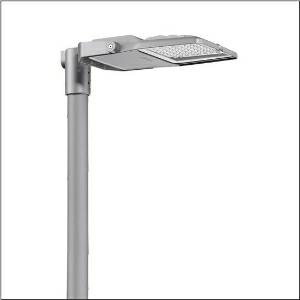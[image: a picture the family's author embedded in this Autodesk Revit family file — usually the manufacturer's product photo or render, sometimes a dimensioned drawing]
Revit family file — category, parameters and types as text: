
# Revit family: floodlight_fl_21_mini___pl61_5xa7776c2c3a_9e20
name_source: partatom
category: Lighting Fixtures
units: mm (PartAtom-declared; Revit-internal decimal feet)

## family parameters
Cut with Voids When Loaded = No
Host = Face
Light Source = No
Part Type = Normal
Room Calculation Point = No
Round Connector Dimension = Use Diameter
Shared = No

## types (1)
- --- (1 x LED, 11960 lm, 89 W, 3000K)
    Apparent Load = 89 VA
    CIE Flux Codes = 33 65 98 100 100
    Color Rendering = 70
    Color Temperature = 3000K
    Default Elevation = 1800 mm
    Description = Floodlight FL 21 mini, floodlight, primary light control with lens, of PMMA, primary optical cover: protective disc, of toughened safety glass, transparent, light distribution: PL61, light emission: direct distribution, installation type: surface-mounted, LED, High Power LED, rated luminous flux: 11.960lm, luminous efficacy: 134lm/W, light colour: 730, colour temperature: 3000K, control gear: Smart Interface (Zhaga), control: flexible luminous flux parameterisation, time-dependent luminous flux control, constant luminous flux control, overheat protection, pre-setting: logarithmic dimming characteristic, with terminal, 6-pole, mains connection: 220..240V, AC, 50/60Hz, start of lifetime: 89W, end of service life: 94W, reduction: 43W, luminaire housing, of diecast aluminium, powder-coated, Siteco® metallic grey (DB 702S), corrosivity category C5 mid according to DIN EN ISO 12944, suitable for swimming pools, chlorine-resistant, sealing non-destructively replaceable, please order mast flange separately, mast bracket, of steel, galvanised, powder-coated, Siteco® metallic grey (DB 702S), Smart Interface below and above, protection rating (complete): IP66, insulation class (complete): insulation class II (safety insulation), certification: CE, ENEC, VDE, protection symbol: D, impact resistance: IK08, permissible operating ambient temperature: -40..+40°C, permissible operating ambient temperature for outdoor applications: -40..+50°C, standard: DIN EN 12944, LABS conformity tested according to VDMA 24364:2018-05, packaging unit: 1 piece

Light Distribution: PL61
    Height = 70 mm
    Lamp = 1 x LED
    Lamp Light Flux = 11960 lm
    Lamp Power = 89 W
    Lamp count = 1
    Length = 485 mm
    Luminous efficacy = 134 lm/W
    Manufacturer = Siteco
    ModVariant = No
    Model = 5XA7776C2C3A
    Number of Poles = 1
    OnlyDefault = Yes
    Power Factor = 1
    Product Name = Floodlight FL 21 mini | PL61
    Product group = floodlight | pylon annexe
    ProductGroupID = 6201
    Protection Class = Protection class II
    Protection Degree = IP 66
    RLX_Detail_Level = 1
    RLX_Emergency_Light_Flux = 0 lm
    RLX_Emergency_Type = 0
    RLX_Emergency_Type_DB = No
    RlxData = <blob elided: 101025 chars, md5=c9580dfd>
    Socket = socket
    Standby Power = 0 W
    System Light Flux = 11960 lm
    System Power = 89 W
    Type Comments = factory setting: luminous flux: 100 % | dim-lin: 254 | 456 mA
    Type Image = l_1007125.jpg
    URL = http://relux.com
    VarID = @adj_193463
    Voltage = 0 V
    Weight = 0.00 kg
    Width = 337 mm

## geometry (parser evidence)
native form markers: Blend x4, Sweep x14
no freeform markers — native parametric forms only
